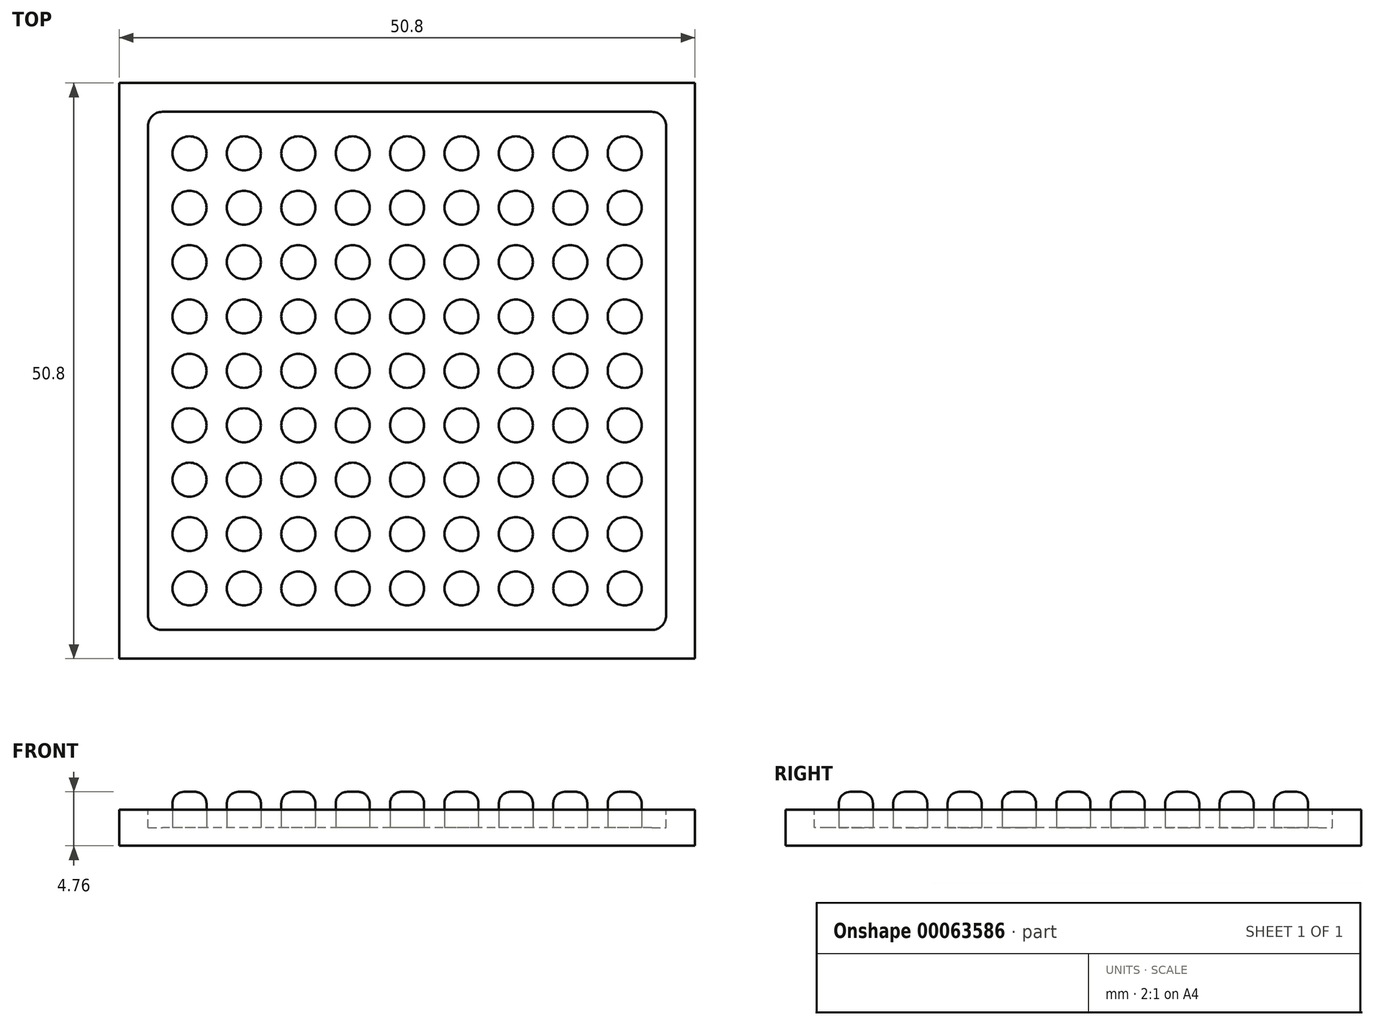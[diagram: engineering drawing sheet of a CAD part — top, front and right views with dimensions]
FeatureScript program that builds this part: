
annotation { "Feature Type Name" : "Feature", "Feature Type Description" : "" }
export const myFeature = defineFeature(function(context is Context, id is Id, definition is map)
    precondition{}
    {
        {
            var Q0;
            Q0=qCreatedBy(makeId("Top.planeOp"),FACE);
            var sketch = newSketch(context, id + "F0", { "sketchPlane" : qUnion([Q0])});
            skLineSegment(sketch, "E0.rect.bottom", {"start": v(25.4, 25.4) * mm, "end": v(-25.4, 25.4) * mm});
            skLineSegment(sketch, "E0.rect.top", {"start": v(25.4, -25.4) * mm, "end": v(-25.4, -25.4) * mm});
            skLineSegment(sketch, "E0.rect.left", {"start": v(25.4, 25.4) * mm, "end": v(25.4, -25.4) * mm});
            skLineSegment(sketch, "E0.rect.right", {"start": v(-25.4, 25.4) * mm, "end": v(-25.4, -25.4) * mm});
            skPoint(sketch, "E0.rect.middle", {"position": v(0, 0) * mm});
            skSolve(sketch);
        }
        {
            var Q0;
            Q0=makeQuery(id+"F0.imprint","IMPRINT",FACE,{"disambiguationData":[TD([[makeQuery(id+"F0.imprint","IMPRINT",EDGE,{"derivedFrom":sQuery(id+"F0.wireOp",EDGE,"E0.rect.bottom")}),1.0]])]});
            extrude(context, id + "F1", {"entities" : qUnion([Q0]), "depth" : 3.17 * mm});
        }
        {
            var Q0;
            Q0=makeQuery(id+"F1.opExtrude","CAP_FACE",FACE,{"disambiguationData":[OSD([sQuery(id+"F0.wireOp",EDGE,"E0.rect.bottom"),sQuery(id+"F0.wireOp",EDGE,"E0.rect.top"),sQuery(id+"F0.wireOp",EDGE,"E0.rect.left"),sQuery(id+"F0.wireOp",EDGE,"E0.rect.right")])],"isStart":false});
            var sketch = newSketch(context, id + "F2", { "sketchPlane" : qUnion([Q0])});
            skLineSegment(sketch, "E1.rect.bottom", {"start": v(22.86, 22.86) * mm, "end": v(-22.86, 22.86) * mm});
            skLineSegment(sketch, "E1.rect.top", {"start": v(22.86, -22.86) * mm, "end": v(-22.86, -22.86) * mm});
            skLineSegment(sketch, "E1.rect.left", {"start": v(22.86, 22.86) * mm, "end": v(22.86, -22.86) * mm});
            skLineSegment(sketch, "E1.rect.right", {"start": v(-22.86, 22.86) * mm, "end": v(-22.86, -22.86) * mm});
            skPoint(sketch, "E1.rect.middle", {"position": v(0, 0) * mm});
            skSolve(sketch);
        }
        {
            var Q0;
            Q0=makeQuery(id+"F2.imprint","IMPRINT",FACE,{"disambiguationData":[TD([[makeQuery(id+"F2.imprint","IMPRINT",EDGE,{"derivedFrom":sQuery(id+"F2.wireOp",EDGE,"E1.rect.bottom")}),1.0]])]});
            extrude(context, id + "F3", {"entities" : qUnion([Q0]), "operationType" : NewBodyOperationType.REMOVE, "oppositeDirection" : true, "depth" : 1.59 * mm});
        }
        {
            var Q0;
            Q0=makeQuery(id+"F3.boolean.opBoolean","COPY",EDGE,{"derivedFrom":makeQuery(id+"F3.opExtrude","SWEPT_EDGE",EDGE,{"disambiguationData":[OSD([sQuery(id+"F2.wireOp",EDGE,"E1.rect.bottom"),sQuery(id+"F2.wireOp",EDGE,"E1.rect.right")])]})});
            var Q1;
            Q1=makeQuery(id+"F3.boolean.opBoolean","COPY",EDGE,{"derivedFrom":makeQuery(id+"F3.opExtrude","SWEPT_EDGE",EDGE,{"disambiguationData":[OSD([sQuery(id+"F2.wireOp",EDGE,"E1.rect.top"),sQuery(id+"F2.wireOp",EDGE,"E1.rect.left")])]})});
            var Q2;
            Q2=makeQuery(id+"F3.boolean.opBoolean","COPY",EDGE,{"derivedFrom":makeQuery(id+"F3.opExtrude","SWEPT_EDGE",EDGE,{"disambiguationData":[OSD([sQuery(id+"F2.wireOp",EDGE,"E1.rect.bottom"),sQuery(id+"F2.wireOp",EDGE,"E1.rect.left")])]})});
            var Q3;
            Q3=makeQuery(id+"F3.boolean.opBoolean","COPY",EDGE,{"derivedFrom":makeQuery(id+"F3.opExtrude","SWEPT_EDGE",EDGE,{"disambiguationData":[OSD([sQuery(id+"F2.wireOp",EDGE,"E1.rect.top"),sQuery(id+"F2.wireOp",EDGE,"E1.rect.right")])]})});
            fillet(context, id + "F4", {"entities" : qUnion([Q0, Q1, Q2, Q3]), "radius" : 1.27 * mm, "tangentPropagation" : true, "allowEdgeOverflow" : false});
        }
        {
            var Q0;
            Q0=makeQuery(id+"F3.boolean.opBoolean","COPY",FACE,{"derivedFrom":makeQuery(id+"F3.opExtrude","CAP_FACE",FACE,{"disambiguationData":[OSD([sQuery(id+"F2.wireOp",EDGE,"E1.rect.bottom"),sQuery(id+"F2.wireOp",EDGE,"E1.rect.top"),sQuery(id+"F2.wireOp",EDGE,"E1.rect.left"),sQuery(id+"F2.wireOp",EDGE,"E1.rect.right")])],"isStart":false})});
            var sketch = newSketch(context, id + "F5", { "sketchPlane" : qUnion([Q0])});
            skCircle(sketch, "E2", {"center": v(19.2, 19.2) * mm, "radius": 1.5 * mm});
            skCircle(sketch, "E3.0.1.0", {"center": v(19.2, 14.4) * mm, "radius": 1.5 * mm});
            skCircle(sketch, "E3.0.2.0", {"center": v(19.2, 9.6) * mm, "radius": 1.5 * mm});
            skCircle(sketch, "E3.0.3.0", {"center": v(19.2, 4.8) * mm, "radius": 1.5 * mm});
            skCircle(sketch, "E3.0.4.0", {"center": v(19.2, 0) * mm, "radius": 1.5 * mm});
            skCircle(sketch, "E3.0.5.0", {"center": v(19.2, -4.8) * mm, "radius": 1.5 * mm});
            skCircle(sketch, "E3.0.6.0", {"center": v(19.2, -9.6) * mm, "radius": 1.5 * mm});
            skCircle(sketch, "E3.0.7.0", {"center": v(19.2, -14.4) * mm, "radius": 1.5 * mm});
            skCircle(sketch, "E3.0.8.0", {"center": v(19.2, -19.2) * mm, "radius": 1.5 * mm});
            skCircle(sketch, "E3.1.0.0", {"center": v(14.4, 19.2) * mm, "radius": 1.5 * mm});
            skCircle(sketch, "E3.1.1.0", {"center": v(14.4, 14.4) * mm, "radius": 1.5 * mm});
            skCircle(sketch, "E3.1.2.0", {"center": v(14.4, 9.6) * mm, "radius": 1.5 * mm});
            skCircle(sketch, "E3.1.3.0", {"center": v(14.4, 4.8) * mm, "radius": 1.5 * mm});
            skCircle(sketch, "E3.1.4.0", {"center": v(14.4, 0) * mm, "radius": 1.5 * mm});
            skCircle(sketch, "E3.1.5.0", {"center": v(14.4, -4.8) * mm, "radius": 1.5 * mm});
            skCircle(sketch, "E3.1.6.0", {"center": v(14.4, -9.6) * mm, "radius": 1.5 * mm});
            skCircle(sketch, "E3.1.7.0", {"center": v(14.4, -14.4) * mm, "radius": 1.5 * mm});
            skCircle(sketch, "E3.1.8.0", {"center": v(14.4, -19.2) * mm, "radius": 1.5 * mm});
            skCircle(sketch, "E3.2.0.0", {"center": v(9.6, 19.2) * mm, "radius": 1.5 * mm});
            skCircle(sketch, "E3.2.1.0", {"center": v(9.6, 14.4) * mm, "radius": 1.5 * mm});
            skCircle(sketch, "E3.2.2.0", {"center": v(9.6, 9.6) * mm, "radius": 1.5 * mm});
            skCircle(sketch, "E3.2.3.0", {"center": v(9.6, 4.8) * mm, "radius": 1.5 * mm});
            skCircle(sketch, "E3.2.4.0", {"center": v(9.6, 0) * mm, "radius": 1.5 * mm});
            skCircle(sketch, "E3.2.5.0", {"center": v(9.6, -4.8) * mm, "radius": 1.5 * mm});
            skCircle(sketch, "E3.2.6.0", {"center": v(9.6, -9.6) * mm, "radius": 1.5 * mm});
            skCircle(sketch, "E3.2.7.0", {"center": v(9.6, -14.4) * mm, "radius": 1.5 * mm});
            skCircle(sketch, "E3.2.8.0", {"center": v(9.6, -19.2) * mm, "radius": 1.5 * mm});
            skCircle(sketch, "E3.3.0.0", {"center": v(4.8, 19.2) * mm, "radius": 1.5 * mm});
            skCircle(sketch, "E3.3.1.0", {"center": v(4.8, 14.4) * mm, "radius": 1.5 * mm});
            skCircle(sketch, "E3.3.2.0", {"center": v(4.8, 9.6) * mm, "radius": 1.5 * mm});
            skCircle(sketch, "E3.3.3.0", {"center": v(4.8, 4.8) * mm, "radius": 1.5 * mm});
            skCircle(sketch, "E3.3.4.0", {"center": v(4.8, 0) * mm, "radius": 1.5 * mm});
            skCircle(sketch, "E3.3.5.0", {"center": v(4.8, -4.8) * mm, "radius": 1.5 * mm});
            skCircle(sketch, "E3.3.6.0", {"center": v(4.8, -9.6) * mm, "radius": 1.5 * mm});
            skCircle(sketch, "E3.3.7.0", {"center": v(4.8, -14.4) * mm, "radius": 1.5 * mm});
            skCircle(sketch, "E3.3.8.0", {"center": v(4.8, -19.2) * mm, "radius": 1.5 * mm});
            skCircle(sketch, "E3.4.0.0", {"center": v(0, 19.2) * mm, "radius": 1.5 * mm});
            skCircle(sketch, "E3.4.1.0", {"center": v(0, 14.4) * mm, "radius": 1.5 * mm});
            skCircle(sketch, "E3.4.2.0", {"center": v(0, 9.6) * mm, "radius": 1.5 * mm});
            skCircle(sketch, "E3.4.3.0", {"center": v(0, 4.8) * mm, "radius": 1.5 * mm});
            skCircle(sketch, "E3.4.4.0", {"center": v(0, 0) * mm, "radius": 1.5 * mm});
            skCircle(sketch, "E3.4.5.0", {"center": v(0, -4.8) * mm, "radius": 1.5 * mm});
            skCircle(sketch, "E3.4.6.0", {"center": v(0, -9.6) * mm, "radius": 1.5 * mm});
            skCircle(sketch, "E3.4.7.0", {"center": v(0, -14.4) * mm, "radius": 1.5 * mm});
            skCircle(sketch, "E3.4.8.0", {"center": v(0, -19.2) * mm, "radius": 1.5 * mm});
            skCircle(sketch, "E3.5.0.0", {"center": v(-4.8, 19.2) * mm, "radius": 1.5 * mm});
            skCircle(sketch, "E3.5.1.0", {"center": v(-4.8, 14.4) * mm, "radius": 1.5 * mm});
            skCircle(sketch, "E3.5.2.0", {"center": v(-4.8, 9.6) * mm, "radius": 1.5 * mm});
            skCircle(sketch, "E3.5.3.0", {"center": v(-4.8, 4.8) * mm, "radius": 1.5 * mm});
            skCircle(sketch, "E3.5.4.0", {"center": v(-4.8, 0) * mm, "radius": 1.5 * mm});
            skCircle(sketch, "E3.5.5.0", {"center": v(-4.8, -4.8) * mm, "radius": 1.5 * mm});
            skCircle(sketch, "E3.5.6.0", {"center": v(-4.8, -9.6) * mm, "radius": 1.5 * mm});
            skCircle(sketch, "E3.5.7.0", {"center": v(-4.8, -14.4) * mm, "radius": 1.5 * mm});
            skCircle(sketch, "E3.5.8.0", {"center": v(-4.8, -19.2) * mm, "radius": 1.5 * mm});
            skCircle(sketch, "E3.6.0.0", {"center": v(-9.6, 19.2) * mm, "radius": 1.5 * mm});
            skCircle(sketch, "E3.6.1.0", {"center": v(-9.6, 14.4) * mm, "radius": 1.5 * mm});
            skCircle(sketch, "E3.6.2.0", {"center": v(-9.6, 9.6) * mm, "radius": 1.5 * mm});
            skCircle(sketch, "E3.6.3.0", {"center": v(-9.6, 4.8) * mm, "radius": 1.5 * mm});
            skCircle(sketch, "E3.6.4.0", {"center": v(-9.6, 0) * mm, "radius": 1.5 * mm});
            skCircle(sketch, "E3.6.5.0", {"center": v(-9.6, -4.8) * mm, "radius": 1.5 * mm});
            skCircle(sketch, "E3.6.6.0", {"center": v(-9.6, -9.6) * mm, "radius": 1.5 * mm});
            skCircle(sketch, "E3.6.7.0", {"center": v(-9.6, -14.4) * mm, "radius": 1.5 * mm});
            skCircle(sketch, "E3.6.8.0", {"center": v(-9.6, -19.2) * mm, "radius": 1.5 * mm});
            skCircle(sketch, "E3.7.0.0", {"center": v(-14.4, 19.2) * mm, "radius": 1.5 * mm});
            skCircle(sketch, "E3.7.1.0", {"center": v(-14.4, 14.4) * mm, "radius": 1.5 * mm});
            skCircle(sketch, "E3.7.2.0", {"center": v(-14.4, 9.6) * mm, "radius": 1.5 * mm});
            skCircle(sketch, "E3.7.3.0", {"center": v(-14.4, 4.8) * mm, "radius": 1.5 * mm});
            skCircle(sketch, "E3.7.4.0", {"center": v(-14.4, 0) * mm, "radius": 1.5 * mm});
            skCircle(sketch, "E3.7.5.0", {"center": v(-14.4, -4.8) * mm, "radius": 1.5 * mm});
            skCircle(sketch, "E3.7.6.0", {"center": v(-14.4, -9.6) * mm, "radius": 1.5 * mm});
            skCircle(sketch, "E3.7.7.0", {"center": v(-14.4, -14.4) * mm, "radius": 1.5 * mm});
            skCircle(sketch, "E3.7.8.0", {"center": v(-14.4, -19.2) * mm, "radius": 1.5 * mm});
            skCircle(sketch, "E3.8.0.0", {"center": v(-19.2, 19.2) * mm, "radius": 1.5 * mm});
            skCircle(sketch, "E3.8.1.0", {"center": v(-19.2, 14.4) * mm, "radius": 1.5 * mm});
            skCircle(sketch, "E3.8.2.0", {"center": v(-19.2, 9.6) * mm, "radius": 1.5 * mm});
            skCircle(sketch, "E3.8.3.0", {"center": v(-19.2, 4.8) * mm, "radius": 1.5 * mm});
            skCircle(sketch, "E3.8.4.0", {"center": v(-19.2, 0) * mm, "radius": 1.5 * mm});
            skCircle(sketch, "E3.8.5.0", {"center": v(-19.2, -4.8) * mm, "radius": 1.5 * mm});
            skCircle(sketch, "E3.8.6.0", {"center": v(-19.2, -9.6) * mm, "radius": 1.5 * mm});
            skCircle(sketch, "E3.8.7.0", {"center": v(-19.2, -14.4) * mm, "radius": 1.5 * mm});
            skCircle(sketch, "E3.8.8.0", {"center": v(-19.2, -19.2) * mm, "radius": 1.5 * mm});
            skLineSegment(sketch, "E3.direction1", {"start": v(19.2, 19.2) * mm, "end": v(14.4, 19.2) * mm, "construction": true});
            skLineSegment(sketch, "E3.direction2", {"start": v(19.2, 19.2) * mm, "end": v(19.2, 14.4) * mm, "construction": true});
            skSolve(sketch);
        }
        {
            var Q0;
            Q0=makeQuery(id+"F5.imprint","IMPRINT",FACE,{"disambiguationData":[TD([[makeQuery(id+"F5.imprint","IMPRINT",EDGE,{"derivedFrom":sQuery(id+"F5.wireOp",EDGE,"E3.8.0.0")}),1.0]])]});
            var Q1;
            Q1=makeQuery(id+"F5.imprint","IMPRINT",FACE,{"disambiguationData":[TD([[makeQuery(id+"F5.imprint","IMPRINT",EDGE,{"derivedFrom":sQuery(id+"F5.wireOp",EDGE,"E3.7.0.0")}),1.0]])]});
            var Q2;
            Q2=makeQuery(id+"F5.imprint","IMPRINT",FACE,{"disambiguationData":[TD([[makeQuery(id+"F5.imprint","IMPRINT",EDGE,{"derivedFrom":sQuery(id+"F5.wireOp",EDGE,"E3.1.8.0")}),1.0]])]});
            var Q3;
            Q3=makeQuery(id+"F5.imprint","IMPRINT",FACE,{"disambiguationData":[TD([[makeQuery(id+"F5.imprint","IMPRINT",EDGE,{"derivedFrom":sQuery(id+"F5.wireOp",EDGE,"E3.3.5.0")}),1.0]])]});
            var Q4;
            Q4=makeQuery(id+"F5.imprint","IMPRINT",FACE,{"disambiguationData":[TD([[makeQuery(id+"F5.imprint","IMPRINT",EDGE,{"derivedFrom":sQuery(id+"F5.wireOp",EDGE,"E3.3.4.0")}),1.0]])]});
            var Q5;
            Q5=makeQuery(id+"F5.imprint","IMPRINT",FACE,{"disambiguationData":[TD([[makeQuery(id+"F5.imprint","IMPRINT",EDGE,{"derivedFrom":sQuery(id+"F5.wireOp",EDGE,"E3.2.4.0")}),1.0]])]});
            var Q6;
            Q6=makeQuery(id+"F5.imprint","IMPRINT",FACE,{"disambiguationData":[TD([[makeQuery(id+"F5.imprint","IMPRINT",EDGE,{"derivedFrom":sQuery(id+"F5.wireOp",EDGE,"E3.1.7.0")}),1.0]])]});
            var Q7;
            Q7=makeQuery(id+"F5.imprint","IMPRINT",FACE,{"disambiguationData":[TD([[makeQuery(id+"F5.imprint","IMPRINT",EDGE,{"derivedFrom":sQuery(id+"F5.wireOp",EDGE,"E3.6.1.0")}),1.0]])]});
            var Q8;
            Q8=makeQuery(id+"F5.imprint","IMPRINT",FACE,{"disambiguationData":[TD([[makeQuery(id+"F5.imprint","IMPRINT",EDGE,{"derivedFrom":sQuery(id+"F5.wireOp",EDGE,"E3.3.7.0")}),1.0]])]});
            var Q9;
            Q9=makeQuery(id+"F5.imprint","IMPRINT",FACE,{"disambiguationData":[TD([[makeQuery(id+"F5.imprint","IMPRINT",EDGE,{"derivedFrom":sQuery(id+"F5.wireOp",EDGE,"E3.2.6.0")}),1.0]])]});
            var Q10;
            Q10=makeQuery(id+"F5.imprint","IMPRINT",FACE,{"disambiguationData":[TD([[makeQuery(id+"F5.imprint","IMPRINT",EDGE,{"derivedFrom":sQuery(id+"F5.wireOp",EDGE,"E3.2.0.0")}),1.0]])]});
            var Q11;
            Q11=makeQuery(id+"F5.imprint","IMPRINT",FACE,{"disambiguationData":[TD([[makeQuery(id+"F5.imprint","IMPRINT",EDGE,{"derivedFrom":sQuery(id+"F5.wireOp",EDGE,"E3.4.5.0")}),1.0]])]});
            var Q12;
            Q12=makeQuery(id+"F5.imprint","IMPRINT",FACE,{"disambiguationData":[TD([[makeQuery(id+"F5.imprint","IMPRINT",EDGE,{"derivedFrom":sQuery(id+"F5.wireOp",EDGE,"E3.4.2.0")}),1.0]])]});
            var Q13;
            Q13=makeQuery(id+"F5.imprint","IMPRINT",FACE,{"disambiguationData":[TD([[makeQuery(id+"F5.imprint","IMPRINT",EDGE,{"derivedFrom":sQuery(id+"F5.wireOp",EDGE,"E3.6.3.0")}),1.0]])]});
            var Q14;
            Q14=makeQuery(id+"F5.imprint","IMPRINT",FACE,{"disambiguationData":[TD([[makeQuery(id+"F5.imprint","IMPRINT",EDGE,{"derivedFrom":sQuery(id+"F5.wireOp",EDGE,"E3.5.3.0")}),1.0]])]});
            var Q15;
            Q15=makeQuery(id+"F5.imprint","IMPRINT",FACE,{"disambiguationData":[TD([[makeQuery(id+"F5.imprint","IMPRINT",EDGE,{"derivedFrom":sQuery(id+"F5.wireOp",EDGE,"E3.6.0.0")}),1.0]])]});
            var Q16;
            Q16=makeQuery(id+"F5.imprint","IMPRINT",FACE,{"disambiguationData":[TD([[makeQuery(id+"F5.imprint","IMPRINT",EDGE,{"derivedFrom":sQuery(id+"F5.wireOp",EDGE,"E3.2.7.0")}),1.0]])]});
            var Q17;
            Q17=makeQuery(id+"F5.imprint","IMPRINT",FACE,{"disambiguationData":[TD([[makeQuery(id+"F5.imprint","IMPRINT",EDGE,{"derivedFrom":sQuery(id+"F5.wireOp",EDGE,"E3.5.4.0")}),1.0]])]});
            var Q18;
            Q18=makeQuery(id+"F5.imprint","IMPRINT",FACE,{"disambiguationData":[TD([[makeQuery(id+"F5.imprint","IMPRINT",EDGE,{"derivedFrom":sQuery(id+"F5.wireOp",EDGE,"E3.3.6.0")}),1.0]])]});
            var Q19;
            Q19=makeQuery(id+"F5.imprint","IMPRINT",FACE,{"disambiguationData":[TD([[makeQuery(id+"F5.imprint","IMPRINT",EDGE,{"derivedFrom":sQuery(id+"F5.wireOp",EDGE,"E3.6.2.0")}),1.0]])]});
            var Q20;
            Q20=makeQuery(id+"F5.imprint","IMPRINT",FACE,{"disambiguationData":[TD([[makeQuery(id+"F5.imprint","IMPRINT",EDGE,{"derivedFrom":sQuery(id+"F5.wireOp",EDGE,"E3.5.5.0")}),1.0]])]});
            var Q21;
            Q21=makeQuery(id+"F5.imprint","IMPRINT",FACE,{"disambiguationData":[TD([[makeQuery(id+"F5.imprint","IMPRINT",EDGE,{"derivedFrom":sQuery(id+"F5.wireOp",EDGE,"E3.4.3.0")}),1.0]])]});
            var Q22;
            Q22=makeQuery(id+"F5.imprint","IMPRINT",FACE,{"disambiguationData":[TD([[makeQuery(id+"F5.imprint","IMPRINT",EDGE,{"derivedFrom":sQuery(id+"F5.wireOp",EDGE,"E3.2.5.0")}),1.0]])]});
            var Q23;
            Q23=makeQuery(id+"F5.imprint","IMPRINT",FACE,{"disambiguationData":[TD([[makeQuery(id+"F5.imprint","IMPRINT",EDGE,{"derivedFrom":sQuery(id+"F5.wireOp",EDGE,"E3.5.2.0")}),1.0]])]});
            var Q24;
            Q24=makeQuery(id+"F5.imprint","IMPRINT",FACE,{"disambiguationData":[TD([[makeQuery(id+"F5.imprint","IMPRINT",EDGE,{"derivedFrom":sQuery(id+"F5.wireOp",EDGE,"E3.2.1.0")}),1.0]])]});
            var Q25;
            Q25=makeQuery(id+"F5.imprint","IMPRINT",FACE,{"disambiguationData":[TD([[makeQuery(id+"F5.imprint","IMPRINT",EDGE,{"derivedFrom":sQuery(id+"F5.wireOp",EDGE,"E3.5.6.0")}),1.0]])]});
            var Q26;
            Q26=makeQuery(id+"F5.imprint","IMPRINT",FACE,{"disambiguationData":[TD([[makeQuery(id+"F5.imprint","IMPRINT",EDGE,{"derivedFrom":sQuery(id+"F5.wireOp",EDGE,"E3.3.8.0")}),1.0]])]});
            var Q27;
            Q27=makeQuery(id+"F5.imprint","IMPRINT",FACE,{"disambiguationData":[TD([[makeQuery(id+"F5.imprint","IMPRINT",EDGE,{"derivedFrom":sQuery(id+"F5.wireOp",EDGE,"E3.6.4.0")}),1.0]])]});
            var Q28;
            Q28=makeQuery(id+"F5.imprint","IMPRINT",FACE,{"disambiguationData":[TD([[makeQuery(id+"F5.imprint","IMPRINT",EDGE,{"derivedFrom":sQuery(id+"F5.wireOp",EDGE,"E3.4.6.0")}),1.0]])]});
            var Q29;
            Q29=makeQuery(id+"F5.imprint","IMPRINT",FACE,{"disambiguationData":[TD([[makeQuery(id+"F5.imprint","IMPRINT",EDGE,{"derivedFrom":sQuery(id+"F5.wireOp",EDGE,"E3.2.8.0")}),1.0]])]});
            var Q30;
            Q30=makeQuery(id+"F5.imprint","IMPRINT",FACE,{"disambiguationData":[TD([[makeQuery(id+"F5.imprint","IMPRINT",EDGE,{"derivedFrom":sQuery(id+"F5.wireOp",EDGE,"E3.2.2.0")}),1.0]])]});
            var Q31;
            Q31=makeQuery(id+"F5.imprint","IMPRINT",FACE,{"disambiguationData":[TD([[makeQuery(id+"F5.imprint","IMPRINT",EDGE,{"derivedFrom":sQuery(id+"F5.wireOp",EDGE,"E3.6.7.0")}),1.0]])]});
            var Q32;
            Q32=makeQuery(id+"F5.imprint","IMPRINT",FACE,{"disambiguationData":[TD([[makeQuery(id+"F5.imprint","IMPRINT",EDGE,{"derivedFrom":sQuery(id+"F5.wireOp",EDGE,"E3.5.0.0")}),1.0]])]});
            var Q33;
            Q33=makeQuery(id+"F5.imprint","IMPRINT",FACE,{"disambiguationData":[TD([[makeQuery(id+"F5.imprint","IMPRINT",EDGE,{"derivedFrom":sQuery(id+"F5.wireOp",EDGE,"E3.5.7.0")}),1.0]])]});
            var Q34;
            Q34=makeQuery(id+"F5.imprint","IMPRINT",FACE,{"disambiguationData":[TD([[makeQuery(id+"F5.imprint","IMPRINT",EDGE,{"derivedFrom":sQuery(id+"F5.wireOp",EDGE,"E3.3.2.0")}),1.0]])]});
            var Q35;
            Q35=makeQuery(id+"F5.imprint","IMPRINT",FACE,{"disambiguationData":[TD([[makeQuery(id+"F5.imprint","IMPRINT",EDGE,{"derivedFrom":sQuery(id+"F5.wireOp",EDGE,"E3.4.0.0")}),1.0]])]});
            var Q36;
            Q36=makeQuery(id+"F5.imprint","IMPRINT",FACE,{"disambiguationData":[TD([[makeQuery(id+"F5.imprint","IMPRINT",EDGE,{"derivedFrom":sQuery(id+"F5.wireOp",EDGE,"E3.6.5.0")}),1.0]])]});
            var Q37;
            Q37=makeQuery(id+"F5.imprint","IMPRINT",FACE,{"disambiguationData":[TD([[makeQuery(id+"F5.imprint","IMPRINT",EDGE,{"derivedFrom":sQuery(id+"F5.wireOp",EDGE,"E3.4.7.0")}),1.0]])]});
            var Q38;
            Q38=makeQuery(id+"F5.imprint","IMPRINT",FACE,{"disambiguationData":[TD([[makeQuery(id+"F5.imprint","IMPRINT",EDGE,{"derivedFrom":sQuery(id+"F5.wireOp",EDGE,"E3.3.0.0")}),1.0]])]});
            var Q39;
            Q39=makeQuery(id+"F5.imprint","IMPRINT",FACE,{"disambiguationData":[TD([[makeQuery(id+"F5.imprint","IMPRINT",EDGE,{"derivedFrom":sQuery(id+"F5.wireOp",EDGE,"E3.2.3.0")}),1.0]])]});
            var Q40;
            Q40=makeQuery(id+"F5.imprint","IMPRINT",FACE,{"disambiguationData":[TD([[makeQuery(id+"F5.imprint","IMPRINT",EDGE,{"derivedFrom":sQuery(id+"F5.wireOp",EDGE,"E3.6.8.0")}),1.0]])]});
            var Q41;
            Q41=makeQuery(id+"F5.imprint","IMPRINT",FACE,{"disambiguationData":[TD([[makeQuery(id+"F5.imprint","IMPRINT",EDGE,{"derivedFrom":sQuery(id+"F5.wireOp",EDGE,"E3.5.1.0")}),1.0]])]});
            var Q42;
            Q42=makeQuery(id+"F5.imprint","IMPRINT",FACE,{"disambiguationData":[TD([[makeQuery(id+"F5.imprint","IMPRINT",EDGE,{"derivedFrom":sQuery(id+"F5.wireOp",EDGE,"E3.5.8.0")}),1.0]])]});
            var Q43;
            Q43=makeQuery(id+"F5.imprint","IMPRINT",FACE,{"disambiguationData":[TD([[makeQuery(id+"F5.imprint","IMPRINT",EDGE,{"derivedFrom":sQuery(id+"F5.wireOp",EDGE,"E3.3.1.0")}),1.0]])]});
            var Q44;
            Q44=makeQuery(id+"F5.imprint","IMPRINT",FACE,{"disambiguationData":[TD([[makeQuery(id+"F5.imprint","IMPRINT",EDGE,{"derivedFrom":sQuery(id+"F5.wireOp",EDGE,"E3.4.1.0")}),1.0]])]});
            var Q45;
            Q45=makeQuery(id+"F5.imprint","IMPRINT",FACE,{"disambiguationData":[TD([[makeQuery(id+"F5.imprint","IMPRINT",EDGE,{"derivedFrom":sQuery(id+"F5.wireOp",EDGE,"E3.4.4.0")}),1.0]])]});
            var Q46;
            Q46=makeQuery(id+"F5.imprint","IMPRINT",FACE,{"disambiguationData":[TD([[makeQuery(id+"F5.imprint","IMPRINT",EDGE,{"derivedFrom":sQuery(id+"F5.wireOp",EDGE,"E3.3.3.0")}),1.0]])]});
            var Q47;
            Q47=makeQuery(id+"F5.imprint","IMPRINT",FACE,{"disambiguationData":[TD([[makeQuery(id+"F5.imprint","IMPRINT",EDGE,{"derivedFrom":sQuery(id+"F5.wireOp",EDGE,"E3.1.0.0")}),1.0]])]});
            var Q48;
            Q48=makeQuery(id+"F5.imprint","IMPRINT",FACE,{"disambiguationData":[TD([[makeQuery(id+"F5.imprint","IMPRINT",EDGE,{"derivedFrom":sQuery(id+"F5.wireOp",EDGE,"E2")}),1.0]])]});
            var Q49;
            Q49=makeQuery(id+"F5.imprint","IMPRINT",FACE,{"disambiguationData":[TD([[makeQuery(id+"F5.imprint","IMPRINT",EDGE,{"derivedFrom":sQuery(id+"F5.wireOp",EDGE,"E3.0.1.0")}),1.0]])]});
            var Q50;
            Q50=makeQuery(id+"F5.imprint","IMPRINT",FACE,{"disambiguationData":[TD([[makeQuery(id+"F5.imprint","IMPRINT",EDGE,{"derivedFrom":sQuery(id+"F5.wireOp",EDGE,"E3.1.1.0")}),1.0]])]});
            var Q51;
            Q51=makeQuery(id+"F5.imprint","IMPRINT",FACE,{"disambiguationData":[TD([[makeQuery(id+"F5.imprint","IMPRINT",EDGE,{"derivedFrom":sQuery(id+"F5.wireOp",EDGE,"E3.1.2.0")}),1.0]])]});
            var Q52;
            Q52=makeQuery(id+"F5.imprint","IMPRINT",FACE,{"disambiguationData":[TD([[makeQuery(id+"F5.imprint","IMPRINT",EDGE,{"derivedFrom":sQuery(id+"F5.wireOp",EDGE,"E3.0.2.0")}),1.0]])]});
            var Q53;
            Q53=makeQuery(id+"F5.imprint","IMPRINT",FACE,{"disambiguationData":[TD([[makeQuery(id+"F5.imprint","IMPRINT",EDGE,{"derivedFrom":sQuery(id+"F5.wireOp",EDGE,"E3.0.3.0")}),1.0]])]});
            var Q54;
            Q54=makeQuery(id+"F5.imprint","IMPRINT",FACE,{"disambiguationData":[TD([[makeQuery(id+"F5.imprint","IMPRINT",EDGE,{"derivedFrom":sQuery(id+"F5.wireOp",EDGE,"E3.1.3.0")}),1.0]])]});
            var Q55;
            Q55=makeQuery(id+"F5.imprint","IMPRINT",FACE,{"disambiguationData":[TD([[makeQuery(id+"F5.imprint","IMPRINT",EDGE,{"derivedFrom":sQuery(id+"F5.wireOp",EDGE,"E3.1.4.0")}),1.0]])]});
            var Q56;
            Q56=makeQuery(id+"F5.imprint","IMPRINT",FACE,{"disambiguationData":[TD([[makeQuery(id+"F5.imprint","IMPRINT",EDGE,{"derivedFrom":sQuery(id+"F5.wireOp",EDGE,"E3.0.4.0")}),1.0]])]});
            var Q57;
            Q57=makeQuery(id+"F5.imprint","IMPRINT",FACE,{"disambiguationData":[TD([[makeQuery(id+"F5.imprint","IMPRINT",EDGE,{"derivedFrom":sQuery(id+"F5.wireOp",EDGE,"E3.0.5.0")}),1.0]])]});
            var Q58;
            Q58=makeQuery(id+"F5.imprint","IMPRINT",FACE,{"disambiguationData":[TD([[makeQuery(id+"F5.imprint","IMPRINT",EDGE,{"derivedFrom":sQuery(id+"F5.wireOp",EDGE,"E3.1.5.0")}),1.0]])]});
            var Q59;
            Q59=makeQuery(id+"F5.imprint","IMPRINT",FACE,{"disambiguationData":[TD([[makeQuery(id+"F5.imprint","IMPRINT",EDGE,{"derivedFrom":sQuery(id+"F5.wireOp",EDGE,"E3.1.6.0")}),1.0]])]});
            var Q60;
            Q60=makeQuery(id+"F5.imprint","IMPRINT",FACE,{"disambiguationData":[TD([[makeQuery(id+"F5.imprint","IMPRINT",EDGE,{"derivedFrom":sQuery(id+"F5.wireOp",EDGE,"E3.0.6.0")}),1.0]])]});
            var Q61;
            Q61=makeQuery(id+"F5.imprint","IMPRINT",FACE,{"disambiguationData":[TD([[makeQuery(id+"F5.imprint","IMPRINT",EDGE,{"derivedFrom":sQuery(id+"F5.wireOp",EDGE,"E3.0.7.0")}),1.0]])]});
            var Q62;
            Q62=makeQuery(id+"F5.imprint","IMPRINT",FACE,{"disambiguationData":[TD([[makeQuery(id+"F5.imprint","IMPRINT",EDGE,{"derivedFrom":sQuery(id+"F5.wireOp",EDGE,"E3.0.8.0")}),1.0]])]});
            var Q63;
            Q63=makeQuery(id+"F5.imprint","IMPRINT",FACE,{"disambiguationData":[TD([[makeQuery(id+"F5.imprint","IMPRINT",EDGE,{"derivedFrom":sQuery(id+"F5.wireOp",EDGE,"E3.4.8.0")}),1.0]])]});
            var Q64;
            Q64=makeQuery(id+"F5.imprint","IMPRINT",FACE,{"disambiguationData":[TD([[makeQuery(id+"F5.imprint","IMPRINT",EDGE,{"derivedFrom":sQuery(id+"F5.wireOp",EDGE,"E3.7.8.0")}),1.0]])]});
            var Q65;
            Q65=makeQuery(id+"F5.imprint","IMPRINT",FACE,{"disambiguationData":[TD([[makeQuery(id+"F5.imprint","IMPRINT",EDGE,{"derivedFrom":sQuery(id+"F5.wireOp",EDGE,"E3.6.6.0")}),1.0]])]});
            var Q66;
            Q66=makeQuery(id+"F5.imprint","IMPRINT",FACE,{"disambiguationData":[TD([[makeQuery(id+"F5.imprint","IMPRINT",EDGE,{"derivedFrom":sQuery(id+"F5.wireOp",EDGE,"E3.7.6.0")}),1.0]])]});
            var Q67;
            Q67=makeQuery(id+"F5.imprint","IMPRINT",FACE,{"disambiguationData":[TD([[makeQuery(id+"F5.imprint","IMPRINT",EDGE,{"derivedFrom":sQuery(id+"F5.wireOp",EDGE,"E3.7.7.0")}),1.0]])]});
            var Q68;
            Q68=makeQuery(id+"F5.imprint","IMPRINT",FACE,{"disambiguationData":[TD([[makeQuery(id+"F5.imprint","IMPRINT",EDGE,{"derivedFrom":sQuery(id+"F5.wireOp",EDGE,"E3.8.8.0")}),1.0]])]});
            var Q69;
            Q69=makeQuery(id+"F5.imprint","IMPRINT",FACE,{"disambiguationData":[TD([[makeQuery(id+"F5.imprint","IMPRINT",EDGE,{"derivedFrom":sQuery(id+"F5.wireOp",EDGE,"E3.8.7.0")}),1.0]])]});
            var Q70;
            Q70=makeQuery(id+"F5.imprint","IMPRINT",FACE,{"disambiguationData":[TD([[makeQuery(id+"F5.imprint","IMPRINT",EDGE,{"derivedFrom":sQuery(id+"F5.wireOp",EDGE,"E3.8.6.0")}),1.0]])]});
            var Q71;
            Q71=makeQuery(id+"F5.imprint","IMPRINT",FACE,{"disambiguationData":[TD([[makeQuery(id+"F5.imprint","IMPRINT",EDGE,{"derivedFrom":sQuery(id+"F5.wireOp",EDGE,"E3.8.5.0")}),1.0]])]});
            var Q72;
            Q72=makeQuery(id+"F5.imprint","IMPRINT",FACE,{"disambiguationData":[TD([[makeQuery(id+"F5.imprint","IMPRINT",EDGE,{"derivedFrom":sQuery(id+"F5.wireOp",EDGE,"E3.7.5.0")}),1.0]])]});
            var Q73;
            Q73=makeQuery(id+"F5.imprint","IMPRINT",FACE,{"disambiguationData":[TD([[makeQuery(id+"F5.imprint","IMPRINT",EDGE,{"derivedFrom":sQuery(id+"F5.wireOp",EDGE,"E3.7.4.0")}),1.0]])]});
            var Q74;
            Q74=makeQuery(id+"F5.imprint","IMPRINT",FACE,{"disambiguationData":[TD([[makeQuery(id+"F5.imprint","IMPRINT",EDGE,{"derivedFrom":sQuery(id+"F5.wireOp",EDGE,"E3.7.3.0")}),1.0]])]});
            var Q75;
            Q75=makeQuery(id+"F5.imprint","IMPRINT",FACE,{"disambiguationData":[TD([[makeQuery(id+"F5.imprint","IMPRINT",EDGE,{"derivedFrom":sQuery(id+"F5.wireOp",EDGE,"E3.7.2.0")}),1.0]])]});
            var Q76;
            Q76=makeQuery(id+"F5.imprint","IMPRINT",FACE,{"disambiguationData":[TD([[makeQuery(id+"F5.imprint","IMPRINT",EDGE,{"derivedFrom":sQuery(id+"F5.wireOp",EDGE,"E3.7.1.0")}),1.0]])]});
            var Q77;
            Q77=makeQuery(id+"F5.imprint","IMPRINT",FACE,{"disambiguationData":[TD([[makeQuery(id+"F5.imprint","IMPRINT",EDGE,{"derivedFrom":sQuery(id+"F5.wireOp",EDGE,"E3.8.1.0")}),1.0]])]});
            var Q78;
            Q78=makeQuery(id+"F5.imprint","IMPRINT",FACE,{"disambiguationData":[TD([[makeQuery(id+"F5.imprint","IMPRINT",EDGE,{"derivedFrom":sQuery(id+"F5.wireOp",EDGE,"E3.8.2.0")}),1.0]])]});
            var Q79;
            Q79=makeQuery(id+"F5.imprint","IMPRINT",FACE,{"disambiguationData":[TD([[makeQuery(id+"F5.imprint","IMPRINT",EDGE,{"derivedFrom":sQuery(id+"F5.wireOp",EDGE,"E3.8.3.0")}),1.0]])]});
            var Q80;
            Q80=makeQuery(id+"F5.imprint","IMPRINT",FACE,{"disambiguationData":[TD([[makeQuery(id+"F5.imprint","IMPRINT",EDGE,{"derivedFrom":sQuery(id+"F5.wireOp",EDGE,"E3.8.4.0")}),1.0]])]});
            extrude(context, id + "F6", {"entities" : qUnion([Q0, Q1, Q2, Q3, Q4, Q5, Q6, Q7, Q8, Q9, Q10, Q11, Q12, Q13, Q14, Q15, Q16, Q17, Q18, Q19, Q20, Q21, Q22, Q23, Q24, Q25, Q26, Q27, Q28, Q29, Q30, Q31, Q32, Q33, Q34, Q35, Q36, Q37, Q38, Q39, Q40, Q41, Q42, Q43, Q44, Q45, Q46, Q47, Q48, Q49, Q50, Q51, Q52, Q53, Q54, Q55, Q56, Q57, Q58, Q59, Q60, Q61, Q62, Q63, Q64, Q65, Q66, Q67, Q68, Q69, Q70, Q71, Q72, Q73, Q74, Q75, Q76, Q77, Q78, Q79, Q80]), "operationType" : NewBodyOperationType.ADD, "depth" : 3.17 * mm});
        }
        {
            var Q0;
            Q0=makeQuery(id+"F6.opExtrude","CAP_FACE",FACE,{"disambiguationData":[OSD([sQuery(id+"F5.wireOp",EDGE,"E3.8.0.0")])],"isStart":false});
            var Q1;
            Q1=makeQuery(id+"F6.opExtrude","CAP_FACE",FACE,{"disambiguationData":[OSD([sQuery(id+"F5.wireOp",EDGE,"E3.7.0.0")])],"isStart":false});
            var Q2;
            Q2=makeQuery(id+"F6.opExtrude","CAP_FACE",FACE,{"disambiguationData":[OSD([sQuery(id+"F5.wireOp",EDGE,"E3.6.0.0")])],"isStart":false});
            var Q3;
            Q3=makeQuery(id+"F6.opExtrude","CAP_FACE",FACE,{"disambiguationData":[OSD([sQuery(id+"F5.wireOp",EDGE,"E3.5.0.0")])],"isStart":false});
            var Q4;
            Q4=makeQuery(id+"F6.opExtrude","CAP_FACE",FACE,{"disambiguationData":[OSD([sQuery(id+"F5.wireOp",EDGE,"E3.4.0.0")])],"isStart":false});
            var Q5;
            Q5=makeQuery(id+"F6.opExtrude","CAP_FACE",FACE,{"disambiguationData":[OSD([sQuery(id+"F5.wireOp",EDGE,"E3.3.0.0")])],"isStart":false});
            var Q6;
            Q6=makeQuery(id+"F6.opExtrude","CAP_FACE",FACE,{"disambiguationData":[OSD([sQuery(id+"F5.wireOp",EDGE,"E3.2.0.0")])],"isStart":false});
            var Q7;
            Q7=makeQuery(id+"F6.opExtrude","CAP_EDGE",EDGE,{"disambiguationData":[OSD([sQuery(id+"F5.wireOp",EDGE,"E3.1.0.0")])],"isStart":false});
            var Q8;
            Q8=makeQuery(id+"F6.opExtrude","CAP_FACE",FACE,{"disambiguationData":[OSD([sQuery(id+"F5.wireOp",EDGE,"E3.1.1.0")])],"isStart":false});
            var Q9;
            Q9=makeQuery(id+"F6.opExtrude","CAP_FACE",FACE,{"disambiguationData":[OSD([sQuery(id+"F5.wireOp",EDGE,"E3.2.1.0")])],"isStart":false});
            var Q10;
            Q10=makeQuery(id+"F6.opExtrude","CAP_FACE",FACE,{"disambiguationData":[OSD([sQuery(id+"F5.wireOp",EDGE,"E3.3.1.0")])],"isStart":false});
            var Q11;
            Q11=makeQuery(id+"F6.opExtrude","CAP_FACE",FACE,{"disambiguationData":[OSD([sQuery(id+"F5.wireOp",EDGE,"E3.4.1.0")])],"isStart":false});
            var Q12;
            Q12=makeQuery(id+"F6.opExtrude","CAP_FACE",FACE,{"disambiguationData":[OSD([sQuery(id+"F5.wireOp",EDGE,"E3.5.1.0")])],"isStart":false});
            var Q13;
            Q13=makeQuery(id+"F6.opExtrude","CAP_FACE",FACE,{"disambiguationData":[OSD([sQuery(id+"F5.wireOp",EDGE,"E3.6.1.0")])],"isStart":false});
            var Q14;
            Q14=makeQuery(id+"F6.opExtrude","CAP_FACE",FACE,{"disambiguationData":[OSD([sQuery(id+"F5.wireOp",EDGE,"E3.7.1.0")])],"isStart":false});
            var Q15;
            Q15=makeQuery(id+"F6.opExtrude","CAP_FACE",FACE,{"disambiguationData":[OSD([sQuery(id+"F5.wireOp",EDGE,"E3.8.1.0")])],"isStart":false});
            var Q16;
            Q16=makeQuery(id+"F6.opExtrude","CAP_FACE",FACE,{"disambiguationData":[OSD([sQuery(id+"F5.wireOp",EDGE,"E3.8.2.0")])],"isStart":false});
            var Q17;
            Q17=makeQuery(id+"F6.opExtrude","CAP_FACE",FACE,{"disambiguationData":[OSD([sQuery(id+"F5.wireOp",EDGE,"E3.7.2.0")])],"isStart":false});
            var Q18;
            Q18=makeQuery(id+"F6.opExtrude","CAP_FACE",FACE,{"disambiguationData":[OSD([sQuery(id+"F5.wireOp",EDGE,"E3.6.2.0")])],"isStart":false});
            var Q19;
            Q19=makeQuery(id+"F6.opExtrude","CAP_FACE",FACE,{"disambiguationData":[OSD([sQuery(id+"F5.wireOp",EDGE,"E3.5.2.0")])],"isStart":false});
            var Q20;
            Q20=makeQuery(id+"F6.opExtrude","CAP_FACE",FACE,{"disambiguationData":[OSD([sQuery(id+"F5.wireOp",EDGE,"E3.4.2.0")])],"isStart":false});
            var Q21;
            Q21=makeQuery(id+"F6.opExtrude","CAP_FACE",FACE,{"disambiguationData":[OSD([sQuery(id+"F5.wireOp",EDGE,"E3.3.2.0")])],"isStart":false});
            var Q22;
            Q22=makeQuery(id+"F6.opExtrude","CAP_FACE",FACE,{"disambiguationData":[OSD([sQuery(id+"F5.wireOp",EDGE,"E3.2.2.0")])],"isStart":false});
            var Q23;
            Q23=makeQuery(id+"F6.opExtrude","CAP_FACE",FACE,{"disambiguationData":[OSD([sQuery(id+"F5.wireOp",EDGE,"E3.1.2.0")])],"isStart":false});
            var Q24;
            Q24=makeQuery(id+"F6.opExtrude","CAP_FACE",FACE,{"disambiguationData":[OSD([sQuery(id+"F5.wireOp",EDGE,"E3.1.3.0")])],"isStart":false});
            var Q25;
            Q25=makeQuery(id+"F6.opExtrude","CAP_FACE",FACE,{"disambiguationData":[OSD([sQuery(id+"F5.wireOp",EDGE,"E3.2.3.0")])],"isStart":false});
            var Q26;
            Q26=makeQuery(id+"F6.opExtrude","CAP_FACE",FACE,{"disambiguationData":[OSD([sQuery(id+"F5.wireOp",EDGE,"E3.3.3.0")])],"isStart":false});
            var Q27;
            Q27=makeQuery(id+"F6.opExtrude","CAP_FACE",FACE,{"disambiguationData":[OSD([sQuery(id+"F5.wireOp",EDGE,"E3.4.3.0")])],"isStart":false});
            var Q28;
            Q28=makeQuery(id+"F6.opExtrude","CAP_FACE",FACE,{"disambiguationData":[OSD([sQuery(id+"F5.wireOp",EDGE,"E3.5.3.0")])],"isStart":false});
            var Q29;
            Q29=makeQuery(id+"F6.opExtrude","CAP_EDGE",EDGE,{"disambiguationData":[OSD([sQuery(id+"F5.wireOp",EDGE,"E3.6.3.0")])],"isStart":false});
            var Q30;
            Q30=makeQuery(id+"F6.opExtrude","CAP_FACE",FACE,{"disambiguationData":[OSD([sQuery(id+"F5.wireOp",EDGE,"E3.7.3.0")])],"isStart":false});
            var Q31;
            Q31=makeQuery(id+"F6.opExtrude","CAP_FACE",FACE,{"disambiguationData":[OSD([sQuery(id+"F5.wireOp",EDGE,"E3.8.3.0")])],"isStart":false});
            var Q32;
            Q32=makeQuery(id+"F6.opExtrude","CAP_FACE",FACE,{"disambiguationData":[OSD([sQuery(id+"F5.wireOp",EDGE,"E3.8.4.0")])],"isStart":false});
            var Q33;
            Q33=makeQuery(id+"F6.opExtrude","CAP_FACE",FACE,{"disambiguationData":[OSD([sQuery(id+"F5.wireOp",EDGE,"E3.7.4.0")])],"isStart":false});
            var Q34;
            Q34=makeQuery(id+"F6.opExtrude","CAP_FACE",FACE,{"disambiguationData":[OSD([sQuery(id+"F5.wireOp",EDGE,"E3.6.4.0")])],"isStart":false});
            var Q35;
            Q35=makeQuery(id+"F6.opExtrude","CAP_FACE",FACE,{"disambiguationData":[OSD([sQuery(id+"F5.wireOp",EDGE,"E3.5.4.0")])],"isStart":false});
            var Q36;
            Q36=makeQuery(id+"F6.opExtrude","CAP_FACE",FACE,{"disambiguationData":[OSD([sQuery(id+"F5.wireOp",EDGE,"E3.4.4.0")])],"isStart":false});
            var Q37;
            Q37=makeQuery(id+"F6.opExtrude","CAP_FACE",FACE,{"disambiguationData":[OSD([sQuery(id+"F5.wireOp",EDGE,"E3.3.4.0")])],"isStart":false});
            var Q38;
            Q38=makeQuery(id+"F6.opExtrude","CAP_FACE",FACE,{"disambiguationData":[OSD([sQuery(id+"F5.wireOp",EDGE,"E3.2.4.0")])],"isStart":false});
            var Q39;
            Q39=makeQuery(id+"F6.opExtrude","CAP_EDGE",EDGE,{"disambiguationData":[OSD([sQuery(id+"F5.wireOp",EDGE,"E2")])],"isStart":false});
            var Q40;
            Q40=makeQuery(id+"F6.opExtrude","CAP_EDGE",EDGE,{"disambiguationData":[OSD([sQuery(id+"F5.wireOp",EDGE,"E3.0.1.0")])],"isStart":false});
            var Q41;
            Q41=makeQuery(id+"F6.opExtrude","CAP_EDGE",EDGE,{"disambiguationData":[OSD([sQuery(id+"F5.wireOp",EDGE,"E3.0.2.0")])],"isStart":false});
            var Q42;
            Q42=makeQuery(id+"F6.opExtrude","CAP_EDGE",EDGE,{"disambiguationData":[OSD([sQuery(id+"F5.wireOp",EDGE,"E3.0.3.0")])],"isStart":false});
            var Q43;
            Q43=makeQuery(id+"F6.opExtrude","CAP_FACE",FACE,{"disambiguationData":[OSD([sQuery(id+"F5.wireOp",EDGE,"E3.0.4.0")])],"isStart":false});
            var Q44;
            Q44=makeQuery(id+"F6.opExtrude","CAP_FACE",FACE,{"disambiguationData":[OSD([sQuery(id+"F5.wireOp",EDGE,"E3.1.4.0")])],"isStart":false});
            var Q45;
            Q45=makeQuery(id+"F6.opExtrude","CAP_FACE",FACE,{"disambiguationData":[OSD([sQuery(id+"F5.wireOp",EDGE,"E3.0.5.0")])],"isStart":false});
            var Q46;
            Q46=makeQuery(id+"F6.opExtrude","CAP_EDGE",EDGE,{"disambiguationData":[OSD([sQuery(id+"F5.wireOp",EDGE,"E3.1.5.0")])],"isStart":false});
            var Q47;
            Q47=makeQuery(id+"F6.opExtrude","CAP_FACE",FACE,{"disambiguationData":[OSD([sQuery(id+"F5.wireOp",EDGE,"E3.2.5.0")])],"isStart":false});
            var Q48;
            Q48=makeQuery(id+"F6.opExtrude","CAP_EDGE",EDGE,{"disambiguationData":[OSD([sQuery(id+"F5.wireOp",EDGE,"E3.3.5.0")])],"isStart":false});
            var Q49;
            Q49=makeQuery(id+"F6.opExtrude","CAP_EDGE",EDGE,{"disambiguationData":[OSD([sQuery(id+"F5.wireOp",EDGE,"E3.4.5.0")])],"isStart":false});
            var Q50;
            Q50=makeQuery(id+"F6.opExtrude","CAP_EDGE",EDGE,{"disambiguationData":[OSD([sQuery(id+"F5.wireOp",EDGE,"E3.5.5.0")])],"isStart":false});
            var Q51;
            Q51=makeQuery(id+"F6.opExtrude","CAP_FACE",FACE,{"disambiguationData":[OSD([sQuery(id+"F5.wireOp",EDGE,"E3.6.5.0")])],"isStart":false});
            var Q52;
            Q52=makeQuery(id+"F6.opExtrude","CAP_EDGE",EDGE,{"disambiguationData":[OSD([sQuery(id+"F5.wireOp",EDGE,"E3.7.5.0")])],"isStart":false});
            var Q53;
            Q53=makeQuery(id+"F6.opExtrude","CAP_FACE",FACE,{"disambiguationData":[OSD([sQuery(id+"F5.wireOp",EDGE,"E3.8.5.0")])],"isStart":false});
            var Q54;
            Q54=makeQuery(id+"F6.opExtrude","CAP_EDGE",EDGE,{"disambiguationData":[OSD([sQuery(id+"F5.wireOp",EDGE,"E3.8.6.0")])],"isStart":false});
            var Q55;
            Q55=makeQuery(id+"F6.opExtrude","CAP_FACE",FACE,{"disambiguationData":[OSD([sQuery(id+"F5.wireOp",EDGE,"E3.7.6.0")])],"isStart":false});
            var Q56;
            Q56=makeQuery(id+"F6.opExtrude","CAP_FACE",FACE,{"disambiguationData":[OSD([sQuery(id+"F5.wireOp",EDGE,"E3.6.6.0")])],"isStart":false});
            var Q57;
            Q57=makeQuery(id+"F6.opExtrude","CAP_FACE",FACE,{"disambiguationData":[OSD([sQuery(id+"F5.wireOp",EDGE,"E3.5.6.0")])],"isStart":false});
            var Q58;
            Q58=makeQuery(id+"F6.opExtrude","CAP_EDGE",EDGE,{"disambiguationData":[OSD([sQuery(id+"F5.wireOp",EDGE,"E3.4.6.0")])],"isStart":false});
            var Q59;
            Q59=makeQuery(id+"F6.opExtrude","CAP_FACE",FACE,{"disambiguationData":[OSD([sQuery(id+"F5.wireOp",EDGE,"E3.3.6.0")])],"isStart":false});
            var Q60;
            Q60=makeQuery(id+"F6.opExtrude","CAP_FACE",FACE,{"disambiguationData":[OSD([sQuery(id+"F5.wireOp",EDGE,"E3.2.6.0")])],"isStart":false});
            var Q61;
            Q61=makeQuery(id+"F6.opExtrude","CAP_FACE",FACE,{"disambiguationData":[OSD([sQuery(id+"F5.wireOp",EDGE,"E3.1.6.0")])],"isStart":false});
            var Q62;
            Q62=makeQuery(id+"F6.opExtrude","CAP_FACE",FACE,{"disambiguationData":[OSD([sQuery(id+"F5.wireOp",EDGE,"E3.0.6.0")])],"isStart":false});
            var Q63;
            Q63=makeQuery(id+"F6.opExtrude","CAP_FACE",FACE,{"disambiguationData":[OSD([sQuery(id+"F5.wireOp",EDGE,"E3.0.7.0")])],"isStart":false});
            var Q64;
            Q64=makeQuery(id+"F6.opExtrude","CAP_EDGE",EDGE,{"disambiguationData":[OSD([sQuery(id+"F5.wireOp",EDGE,"E3.1.7.0")])],"isStart":false});
            var Q65;
            Q65=makeQuery(id+"F6.opExtrude","CAP_FACE",FACE,{"disambiguationData":[OSD([sQuery(id+"F5.wireOp",EDGE,"E3.2.7.0")])],"isStart":false});
            var Q66;
            Q66=makeQuery(id+"F6.opExtrude","CAP_EDGE",EDGE,{"disambiguationData":[OSD([sQuery(id+"F5.wireOp",EDGE,"E3.3.7.0")])],"isStart":false});
            var Q67;
            Q67=makeQuery(id+"F6.opExtrude","CAP_EDGE",EDGE,{"disambiguationData":[OSD([sQuery(id+"F5.wireOp",EDGE,"E3.4.7.0")])],"isStart":false});
            var Q68;
            Q68=makeQuery(id+"F6.opExtrude","CAP_EDGE",EDGE,{"disambiguationData":[OSD([sQuery(id+"F5.wireOp",EDGE,"E3.5.7.0")])],"isStart":false});
            var Q69;
            Q69=makeQuery(id+"F6.opExtrude","CAP_EDGE",EDGE,{"disambiguationData":[OSD([sQuery(id+"F5.wireOp",EDGE,"E3.6.7.0")])],"isStart":false});
            var Q70;
            Q70=makeQuery(id+"F6.opExtrude","CAP_EDGE",EDGE,{"disambiguationData":[OSD([sQuery(id+"F5.wireOp",EDGE,"E3.7.7.0")])],"isStart":false});
            var Q71;
            Q71=makeQuery(id+"F6.opExtrude","CAP_EDGE",EDGE,{"disambiguationData":[OSD([sQuery(id+"F5.wireOp",EDGE,"E3.8.7.0")])],"isStart":false});
            var Q72;
            Q72=makeQuery(id+"F6.opExtrude","CAP_EDGE",EDGE,{"disambiguationData":[OSD([sQuery(id+"F5.wireOp",EDGE,"E3.8.8.0")])],"isStart":false});
            var Q73;
            Q73=makeQuery(id+"F6.opExtrude","CAP_FACE",FACE,{"disambiguationData":[OSD([sQuery(id+"F5.wireOp",EDGE,"E3.7.8.0")])],"isStart":false});
            var Q74;
            Q74=makeQuery(id+"F6.opExtrude","CAP_FACE",FACE,{"disambiguationData":[OSD([sQuery(id+"F5.wireOp",EDGE,"E3.6.8.0")])],"isStart":false});
            var Q75;
            Q75=makeQuery(id+"F6.opExtrude","CAP_FACE",FACE,{"disambiguationData":[OSD([sQuery(id+"F5.wireOp",EDGE,"E3.5.8.0")])],"isStart":false});
            var Q76;
            Q76=makeQuery(id+"F6.opExtrude","CAP_EDGE",EDGE,{"disambiguationData":[OSD([sQuery(id+"F5.wireOp",EDGE,"E3.4.8.0")])],"isStart":false});
            var Q77;
            Q77=makeQuery(id+"F6.opExtrude","CAP_FACE",FACE,{"disambiguationData":[OSD([sQuery(id+"F5.wireOp",EDGE,"E3.3.8.0")])],"isStart":false});
            var Q78;
            Q78=makeQuery(id+"F6.opExtrude","CAP_EDGE",EDGE,{"disambiguationData":[OSD([sQuery(id+"F5.wireOp",EDGE,"E3.2.8.0")])],"isStart":false});
            var Q79;
            Q79=makeQuery(id+"F6.opExtrude","CAP_EDGE",EDGE,{"disambiguationData":[OSD([sQuery(id+"F5.wireOp",EDGE,"E3.1.8.0")])],"isStart":false});
            var Q80;
            Q80=makeQuery(id+"F6.opExtrude","CAP_EDGE",EDGE,{"disambiguationData":[OSD([sQuery(id+"F5.wireOp",EDGE,"E3.0.8.0")])],"isStart":false});
            fillet(context, id + "F7", {"entities" : qUnion([Q0, Q1, Q2, Q3, Q4, Q5, Q6, Q7, Q8, Q9, Q10, Q11, Q12, Q13, Q14, Q15, Q16, Q17, Q18, Q19, Q20, Q21, Q22, Q23, Q24, Q25, Q26, Q27, Q28, Q29, Q30, Q31, Q32, Q33, Q34, Q35, Q36, Q37, Q38, Q39, Q40, Q41, Q42, Q43, Q44, Q45, Q46, Q47, Q48, Q49, Q50, Q51, Q52, Q53, Q54, Q55, Q56, Q57, Q58, Q59, Q60, Q61, Q62, Q63, Q64, Q65, Q66, Q67, Q68, Q69, Q70, Q71, Q72, Q73, Q74, Q75, Q76, Q77, Q78, Q79, Q80]), "radius" : 1.02 * mm, "tangentPropagation" : true, "allowEdgeOverflow" : false});
        }
    });
